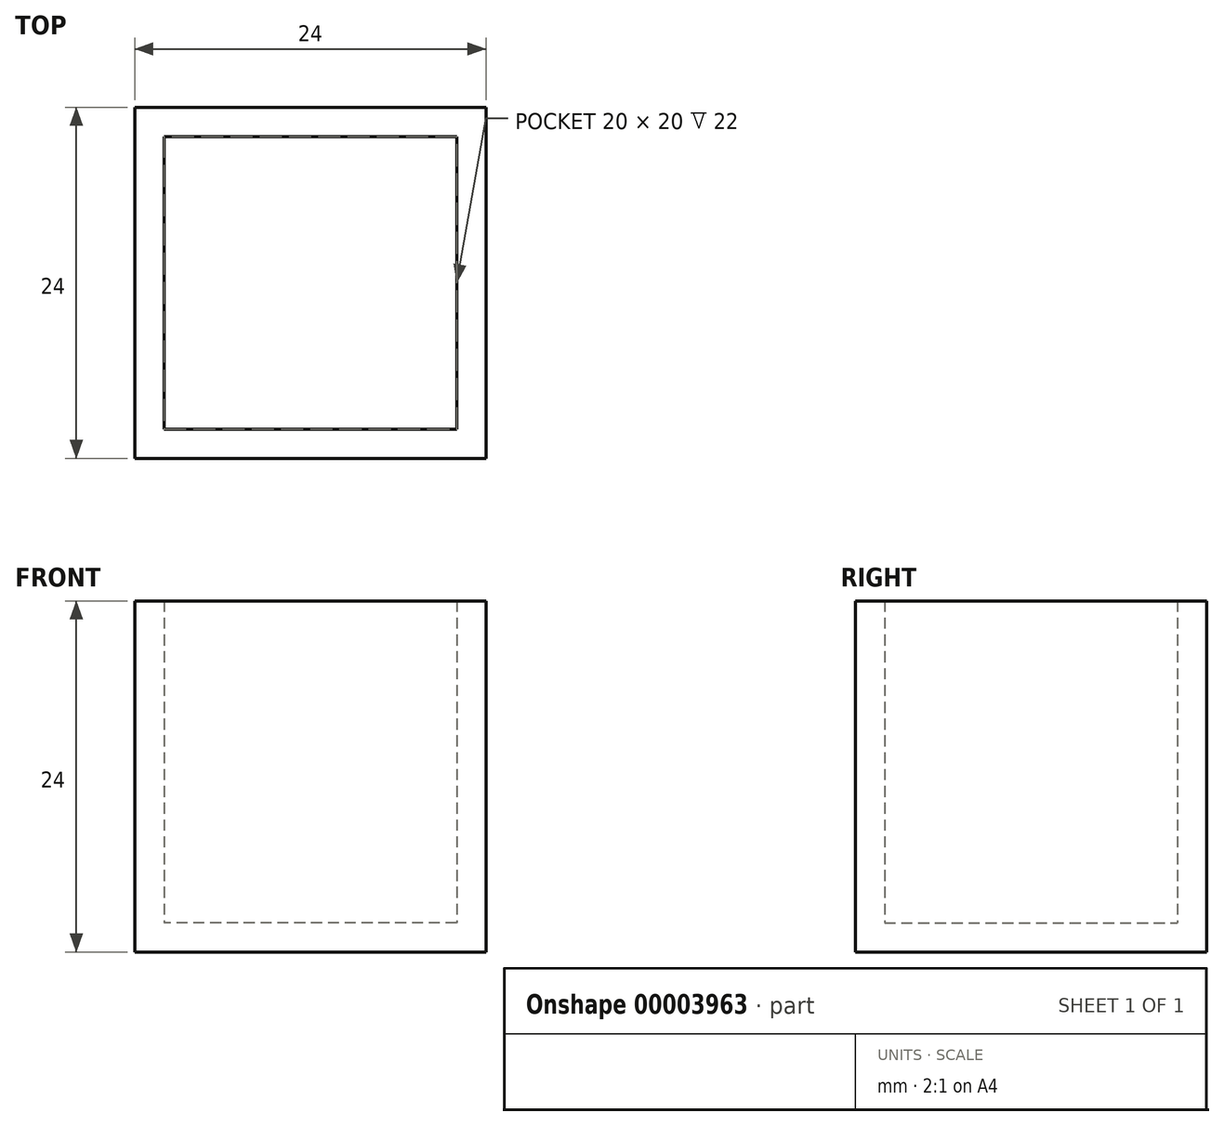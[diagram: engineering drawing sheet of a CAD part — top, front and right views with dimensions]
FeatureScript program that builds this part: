
annotation { "Feature Type Name" : "Feature", "Feature Type Description" : "" }
export const myFeature = defineFeature(function(context is Context, id is Id, definition is map)
    precondition{}
    {
        {
            var Q0;
            Q0=qCreatedBy(makeId("Top.planeOp"),FACE);
            var sketch = newSketch(context, id + "F0", { "sketchPlane" : qUnion([Q0])});
            skLineSegment(sketch, "E0.rect.bottom", {"start": v(12, -12) * mm, "end": v(-12, -12) * mm});
            skLineSegment(sketch, "E0.rect.top", {"start": v(12, 12) * mm, "end": v(-12, 12) * mm});
            skLineSegment(sketch, "E0.rect.left", {"start": v(12, -12) * mm, "end": v(12, 12) * mm});
            skLineSegment(sketch, "E0.rect.right", {"start": v(-12, -12) * mm, "end": v(-12, 12) * mm});
            skPoint(sketch, "E0.rect.middle", {"position": v(0, 0) * mm});
            skSolve(sketch);
        }
        {
            var Q0;
            Q0=makeQuery(id+"F0.imprint","IMPRINT",FACE,{"disambiguationData":[TD([[makeQuery(id+"F0.imprint","IMPRINT",EDGE,{"derivedFrom":sQuery(id+"F0.wireOp",EDGE,"E0.rect.bottom")}),-1.0]])]});
            extrude(context, id + "F1", {"entities" : qUnion([Q0]), "depth" : 24 * mm});
        }
        {
            var Q0;
            Q0=makeQuery(id+"F1.opExtrude","CAP_FACE",FACE,{"disambiguationData":[OSD([sQuery(id+"F0.wireOp",EDGE,"E0.rect.bottom"),sQuery(id+"F0.wireOp",EDGE,"E0.rect.top"),sQuery(id+"F0.wireOp",EDGE,"E0.rect.left"),sQuery(id+"F0.wireOp",EDGE,"E0.rect.right")])],"isStart":false});
            shell(context, id + "F2", {"entities" : qUnion([Q0]), "thickness" : 2 * mm});
        }
    });
